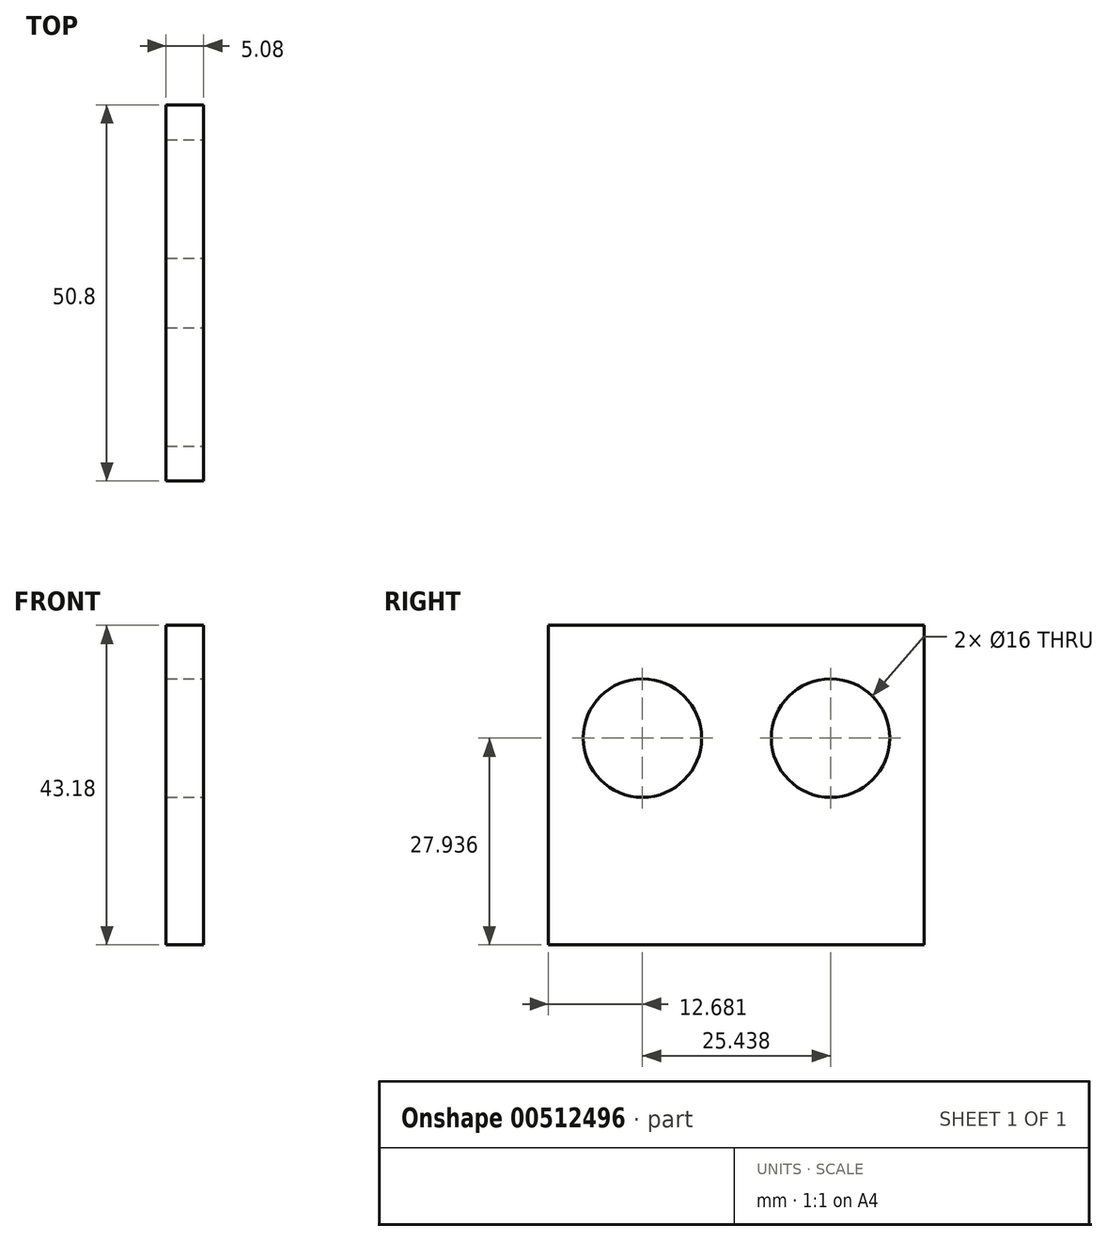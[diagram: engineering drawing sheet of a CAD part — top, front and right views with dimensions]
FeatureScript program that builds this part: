
annotation { "Feature Type Name" : "Feature", "Feature Type Description" : "" }
export const myFeature = defineFeature(function(context is Context, id is Id, definition is map)
    precondition{}
    {
        {
            var Q0;
            Q0=qCreatedBy(makeId("Right.planeOp"),FACE);
            var sketch = newSketch(context, id + "F0", { "sketchPlane" : qUnion([Q0])});
            skLineSegment(sketch, "E0.bottom", {"start": v(-14.24, 24.96) * mm, "end": v(36.56, 24.96) * mm});
            skLineSegment(sketch, "E0.top", {"start": v(-14.24, -18.22) * mm, "end": v(36.56, -18.22) * mm});
            skLineSegment(sketch, "E0.left", {"start": v(-14.24, 24.96) * mm, "end": v(-14.24, -18.22) * mm});
            skLineSegment(sketch, "E0.right", {"start": v(36.56, 24.96) * mm, "end": v(36.56, -18.22) * mm});
            skSolve(sketch);
        }
        {
            var Q0;
            Q0=makeQuery(id+"F0.imprint","IMPRINT",FACE,{"disambiguationData":[TD([[makeQuery(id+"F0.imprint","IMPRINT",EDGE,{"derivedFrom":sQuery(id+"F0.wireOp",EDGE,"E0.bottom")}),-1.0]])]});
            extrude(context, id + "F1", {"entities" : qUnion([Q0]), "depth" : 5.08 * mm});
        }
        {
            var Q0;
            Q0=makeQuery(id+"F1.opExtrude","CAP_FACE",FACE,{"disambiguationData":[OSD([sQuery(id+"F0.wireOp",EDGE,"E0.bottom"),sQuery(id+"F0.wireOp",EDGE,"E0.top"),sQuery(id+"F0.wireOp",EDGE,"E0.left"),sQuery(id+"F0.wireOp",EDGE,"E0.right")])],"isStart":false});
            var sketch = newSketch(context, id + "F2", { "sketchPlane" : qUnion([Q0])});
            skCircle(sketch, "E1", {"center": v(-1.56, 9.72) * mm, "radius": 8 * mm});
            skCircle(sketch, "E2", {"center": v(23.88, 9.72) * mm, "radius": 8 * mm});
            skLineSegment(sketch, "E3", {"start": v(11.16, 24.96) * mm, "end": v(11.16, -6.26) * mm, "construction": true});
            skSolve(sketch);
        }
        {
            var Q0;
            Q0=makeQuery(id+"F2.imprint","IMPRINT",FACE,{"disambiguationData":[TD([[makeQuery(id+"F2.imprint","IMPRINT",EDGE,{"derivedFrom":sQuery(id+"F2.wireOp",EDGE,"E2")}),1.0]])]});
            var Q1;
            Q1=makeQuery(id+"F2.imprint","IMPRINT",FACE,{"disambiguationData":[TD([[makeQuery(id+"F2.imprint","IMPRINT",EDGE,{"derivedFrom":sQuery(id+"F2.wireOp",EDGE,"E1")}),1.0]])]});
            extrude(context, id + "F3", {"entities" : qUnion([Q0, Q1]), "operationType" : NewBodyOperationType.REMOVE, "oppositeDirection" : true, "depth" : 25.4 * mm});
        }
    });
